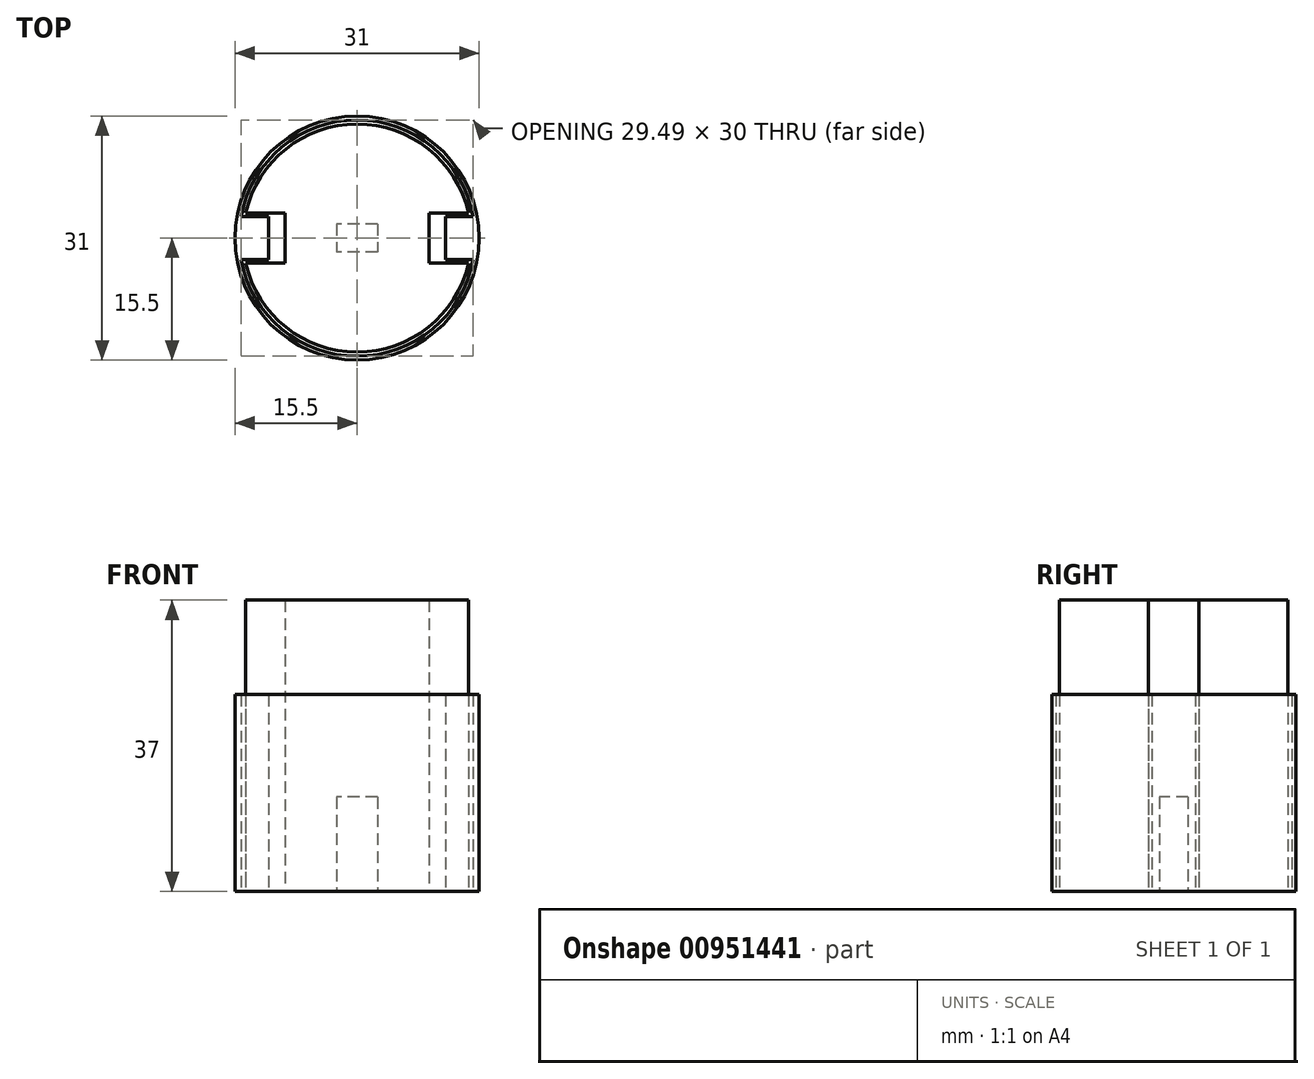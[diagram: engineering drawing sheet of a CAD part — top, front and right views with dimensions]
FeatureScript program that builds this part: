
annotation { "Feature Type Name" : "Feature", "Feature Type Description" : "" }
export const myFeature = defineFeature(function(context is Context, id is Id, definition is map)
    precondition{}
    {
        {
            var Q0;
            Q0=qCreatedBy(makeId("Top.planeOp"),FACE);
            var sketch = newSketch(context, id + "F0", { "sketchPlane" : qUnion([Q0])});
            skCircle(sketch, "E0", {"center": v(0, 0) * mm, "radius": 15 * mm});
            skLineSegment(sketch, "E1", {"start": v(-14.75, 2.75) * mm, "end": v(-11.25, 2.75) * mm});
            skLineSegment(sketch, "E2", {"start": v(-11.25, 2.75) * mm, "end": v(-11.25, 0) * mm});
            skLineSegment(sketch, "E3", {"start": v(-11.25, 0) * mm, "end": v(-11.25, -2.75) * mm});
            skLineSegment(sketch, "E4", {"start": v(-11.25, -2.75) * mm, "end": v(-14.75, -2.75) * mm});
            skLineSegment(sketch, "E5", {"start": v(14.75, 2.75) * mm, "end": v(11.25, 2.75) * mm});
            skLineSegment(sketch, "E6", {"start": v(11.25, 2.75) * mm, "end": v(11.25, 0) * mm});
            skLineSegment(sketch, "E7", {"start": v(11.25, 0) * mm, "end": v(11.25, -2.75) * mm});
            skLineSegment(sketch, "E8", {"start": v(11.25, -2.75) * mm, "end": v(14.75, -2.75) * mm});
            skCircle(sketch, "E9", {"center": v(0, 0) * mm, "radius": 15.5 * mm});
            skSolve(sketch);
        }
        {
            var Q0;
            Q0=makeQuery(id+"F0.imprint","IMPRINT",FACE,{"disambiguationData":[TD([[makeQuery(id+"F0.imprint","IMPRINT",EDGE,{"derivedFrom":sQuery(id+"F0.wireOp",EDGE,"E9")}),1.0]])]});
            var Q1;
            {var subQ0=sQuery(id+"F0.wireOp",EDGE,"E1");Q1=makeQuery(id+"F0.imprint","IMPRINT",FACE,{"disambiguationData":[TD([[makeQuery(id+"F0.imprint","IMPRINT",EDGE,{"derivedFrom":subQ0}),-1.0]])]});}
            var Q2;
            {var subQ0=sQuery(id+"F0.wireOp",EDGE,"E5");Q2=makeQuery(id+"F0.imprint","IMPRINT",FACE,{"disambiguationData":[TD([[makeQuery(id+"F0.imprint","IMPRINT",EDGE,{"derivedFrom":subQ0}),1.0]])]});}
            extrude(context, id + "F1", {"entities" : qUnion([Q0, Q1, Q2]), "depth" : 25 * mm, "offsetDistance" : 25 * mm});
        }
        {
            var Q0;
            Q0=qCreatedBy(makeId("Top.planeOp"),FACE);
            var sketch = newSketch(context, id + "F2", { "sketchPlane" : qUnion([Q0])});
            skCircle(sketch, "E10", {"center": v(0, 0) * mm, "radius": 14.5 * mm});
            skLineSegment(sketch, "E11", {"start": v(-14.14, 3.2) * mm, "end": v(-9.14, 3.2) * mm});
            skLineSegment(sketch, "E12", {"start": v(-9.14, 3.2) * mm, "end": v(-9.14, 0) * mm});
            skLineSegment(sketch, "E13", {"start": v(-9.14, 0) * mm, "end": v(-9.14, -3.2) * mm});
            skLineSegment(sketch, "E14", {"start": v(-9.14, -3.2) * mm, "end": v(-14.14, -3.2) * mm});
            skLineSegment(sketch, "E15", {"start": v(14.14, 3.2) * mm, "end": v(9.14, 3.2) * mm});
            skLineSegment(sketch, "E16", {"start": v(9.14, 3.2) * mm, "end": v(9.14, 0) * mm});
            skLineSegment(sketch, "E17", {"start": v(9.14, 0) * mm, "end": v(9.14, -3.2) * mm});
            skLineSegment(sketch, "E18", {"start": v(9.14, -3.2) * mm, "end": v(14.14, -3.2) * mm});
            skLineSegment(sketch, "E19.bottom", {"start": v(2.6, 1.8) * mm, "end": v(-2.6, 1.8) * mm});
            skLineSegment(sketch, "E19.top", {"start": v(2.6, -1.8) * mm, "end": v(-2.6, -1.8) * mm});
            skLineSegment(sketch, "E19.left", {"start": v(2.6, 1.8) * mm, "end": v(2.6, -1.8) * mm});
            skLineSegment(sketch, "E19.right", {"start": v(-2.6, 1.8) * mm, "end": v(-2.6, -1.8) * mm});
            skSolve(sketch);
        }
        {
            var Q0;
            {var subQ3=sQuery(id+"F2.wireOp",EDGE,"E11");Q0=makeQuery(id+"F2.imprint","IMPRINT",FACE,{"disambiguationData":[TD([[makeQuery(id+"F2.imprint","IMPRINT",EDGE,{"derivedFrom":subQ3}),1.0]])]});}
            extrude(context, id + "F3", {"entities" : qUnion([Q0]), "depth" : 12 * mm, "offsetDistance" : 25 * mm});
        }
        {
            var Q0;
            Q0=makeQuery(id+"F3.opExtrude","CAP_FACE",FACE,{"disambiguationData":[OSD([sQuery(id+"F2.wireOp",EDGE,"E10"),sQuery(id+"F2.wireOp",EDGE,"E11"),sQuery(id+"F2.wireOp",EDGE,"E12"),sQuery(id+"F2.wireOp",EDGE,"E13"),sQuery(id+"F2.wireOp",EDGE,"E14"),sQuery(id+"F2.wireOp",EDGE,"E15"),sQuery(id+"F2.wireOp",EDGE,"E16"),sQuery(id+"F2.wireOp",EDGE,"E17"),sQuery(id+"F2.wireOp",EDGE,"E18"),sQuery(id+"F2.wireOp",EDGE,"E19.bottom"),sQuery(id+"F2.wireOp",EDGE,"E19.top"),sQuery(id+"F2.wireOp",EDGE,"E19.left"),sQuery(id+"F2.wireOp",EDGE,"E19.right")])],"isStart":false});
            var sketch = newSketch(context, id + "F4", { "sketchPlane" : qUnion([Q0])});
            skCircle(sketch, "E20", {"center": v(0, 0) * mm, "radius": 14.5 * mm});
            skSolve(sketch);
        }
        {
            var Q0;
            {var subQ4=makeQuery(id+"F3.opExtrude","CAP_EDGE",EDGE,{"disambiguationData":[OSD([sQuery(id+"F2.wireOp",EDGE,"E11")])],"isStart":false});Q0=makeQuery(id+"F4.imprint","IMPRINT",FACE,{"disambiguationData":[TD([[makeQuery(id+"F4.imprint","IMPRINT",EDGE,{"derivedFrom":subQ4}),1.0]])]});}
            var Q1;
            Q1=makeQuery(id+"F4.imprint","IMPRINT",FACE,{"disambiguationData":[TD([[makeQuery(id+"F4.imprint","IMPRINT",EDGE,{"derivedFrom":makeQuery(id+"F3.opExtrude","CAP_EDGE",EDGE,{"disambiguationData":[OSD([sQuery(id+"F2.wireOp",EDGE,"E19.bottom")])],"isStart":false})}),1.0]])]});
            extrude(context, id + "F5", {"entities" : qUnion([Q0, Q1]), "operationType" : NewBodyOperationType.ADD, "depth" : 25 * mm, "offsetDistance" : 25 * mm});
        }
    });
